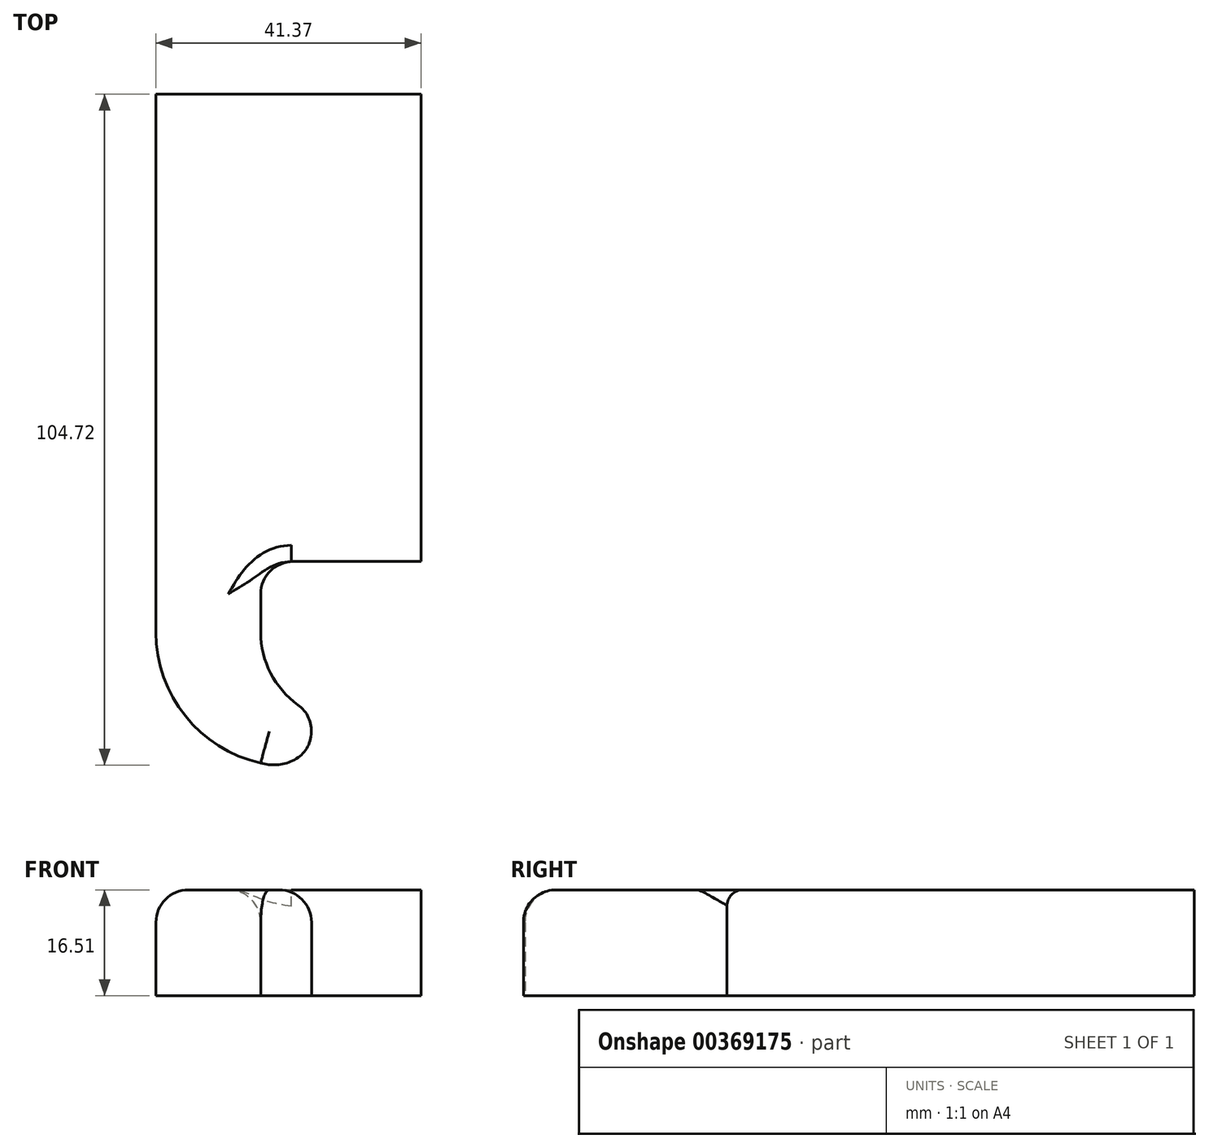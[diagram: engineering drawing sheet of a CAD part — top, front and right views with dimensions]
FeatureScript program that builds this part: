
annotation { "Feature Type Name" : "Feature", "Feature Type Description" : "" }
export const myFeature = defineFeature(function(context is Context, id is Id, definition is map)
    precondition{}
    {
        {
            var Q0;
            Q0=qCreatedBy(makeId("Top.planeOp"),FACE);
            var sketch = newSketch(context, id + "F0", { "sketchPlane" : qUnion([Q0])});
            skLineSegment(sketch, "E0.bottom", {"start": v(0, 0) * mm, "end": v(-16.36, 0) * mm});
            skLineSegment(sketch, "E0.top", {"start": v(0, -37.8) * mm, "end": v(-16.36, -37.8) * mm});
            skLineSegment(sketch, "E0.left", {"start": v(0, 0) * mm, "end": v(0, -37.8) * mm});
            skLineSegment(sketch, "E0.right", {"start": v(-16.36, 0) * mm, "end": v(-16.36, -37.8) * mm});
            skArc(sketch, "E1", {"start": v(-16.36, -37.8) * mm, "mid": v(-11.77, -50.87) * mm, "end": v(0, -58.18) * mm});
            skArc(sketch, "E2", {"start": v(0, -37.8) * mm, "mid": v(4.25, -47.8) * mm, "end": v(14.4, -51.7) * mm});
            skArc(sketch, "E3", {"start": v(0, -58.18) * mm, "mid": v(6.47, -56.9) * mm, "end": v(9, -50.82) * mm});
            skLineSegment(sketch, "E4.bottom", {"start": v(-16.36, -26.72) * mm, "end": v(25.01, -26.72) * mm});
            skLineSegment(sketch, "E4.top", {"start": v(-16.36, 46.23) * mm, "end": v(25.01, 46.23) * mm});
            skLineSegment(sketch, "E4.left", {"start": v(-16.36, -26.72) * mm, "end": v(-16.36, 46.23) * mm});
            skLineSegment(sketch, "E4.right", {"start": v(25.01, -26.72) * mm, "end": v(25.01, 46.23) * mm});
            skSolve(sketch);
        }
        {
            var Q0;
            {var subQ0=sQuery(id+"F0.wireOp",EDGE,"E0.top");Q0=makeQuery(id+"F0.imprint","IMPRINT",FACE,{"disambiguationData":[TD([[makeQuery(id+"F0.imprint","IMPRINT",EDGE,{"derivedFrom":subQ0}),1.0]])]});}
            var Q1;
            Q1=makeQuery(id+"F0.imprint","IMPRINT",FACE,{"disambiguationData":[TD([[makeQuery(id+"F0.imprint","IMPRINT",EDGE,{"derivedFrom":sQuery(id+"F0.wireOp",EDGE,"E0.bottom")}),1.0]])]});
            var Q2;
            {var subQ0=sQuery(id+"F0.wireOp",EDGE,"E0.top");Q2=makeQuery(id+"F0.imprint","IMPRINT",FACE,{"disambiguationData":[TD([[makeQuery(id+"F0.imprint","IMPRINT",EDGE,{"derivedFrom":subQ0}),-1.0]])]});}
            var Q3;
            {var subQ4=sQuery(id+"F0.wireOp",EDGE,"E0.bottom");Q3=makeQuery(id+"F0.imprint","IMPRINT",FACE,{"disambiguationData":[TD([[makeQuery(id+"F0.imprint","IMPRINT",EDGE,{"derivedFrom":subQ4}),-1.0]])]});}
            extrude(context, id + "F1", {"entities" : qUnion([Q0, Q1, Q2, Q3]), "depth" : 16.5 * mm, "offsetDistance" : 25.4 * mm});
        }
        {
            var Q0;
            Q0=makeQuery(id+"F1.opExtrude","SWEPT_EDGE",EDGE,{"disambiguationData":[OSD([sQuery(id+"F0.wireOp",EDGE,"E2"),sQuery(id+"F0.wireOp",EDGE,"E3")])]});
            fillet(context, id + "F2", {"entities" : qUnion([Q0]), "tangentPropagation" : true, "radius" : 5.08 * mm, "defaultsChanged" : false, "vertexSettings" : [], "allowEdgeOverflow" : false});
        }
        {
            var Q0;
            {var subQ0=sQuery(id+"F0.wireOp",EDGE,"E3");var subQ1=sQuery(id+"F0.wireOp",EDGE,"E2");Q0=makeQuery(id+"F2.opFillet","BLEND_EDGE",EDGE,{"blendedFrom":[makeQuery(id+"F1.opExtrude","SWEPT_EDGE",EDGE,{"disambiguationData":[OSD([subQ1,subQ0])]}),makeQuery(id+"F1.opExtrude","CAP_FACE",FACE,{"disambiguationData":[OSD([sQuery(id+"F0.wireOp",EDGE,"E0.bottom"),sQuery(id+"F0.wireOp",EDGE,"E0.left"),sQuery(id+"F0.wireOp",EDGE,"E0.right"),sQuery(id+"F0.wireOp",EDGE,"E1"),subQ1,subQ0])],"isStart":false})],"blendedInto":[makeQuery(id+"F1.opExtrude","CAP_FACE",FACE,{"disambiguationData":[OSD([sQuery(id+"F0.wireOp",EDGE,"E0.bottom"),sQuery(id+"F0.wireOp",EDGE,"E0.left"),sQuery(id+"F0.wireOp",EDGE,"E0.right"),sQuery(id+"F0.wireOp",EDGE,"E1"),subQ1,subQ0])],"isStart":false})]});}
            fillet(context, id + "F3", {"entities" : qUnion([Q0]), "tangentPropagation" : true, "radius" : 5.08 * mm, "defaultsChanged" : true, "vertexSettings" : [], "allowEdgeOverflow" : false});
        }
        {
            var Q0;
            Q0=makeQuery(id+"F1.opExtrude","SWEPT_EDGE",EDGE,{"disambiguationData":[OSD([sQuery(id+"F0.wireOp",EDGE,"E0.left"),sQuery(id+"F0.wireOp",EDGE,"E4.bottom")])]});
            fillet(context, id + "F4", {"entities" : qUnion([Q0]), "tangentPropagation" : true, "radius" : 5.08 * mm, "defaultsChanged" : false, "vertexSettings" : [], "allowEdgeOverflow" : false});
        }
        {
            var Q0;
            Q0=makeQuery(id+"F1.opExtrude","CAP_EDGE",EDGE,{"disambiguationData":[OSD([sQuery(id+"F0.wireOp",EDGE,"E4.bottom")])],"isStart":false});
            fillet(context, id + "F5", {"entities" : qUnion([Q0]), "tangentPropagation" : true, "radius" : 2.54 * mm, "defaultsChanged" : true, "vertexSettings" : [], "allowEdgeOverflow" : false});
        }
    });
